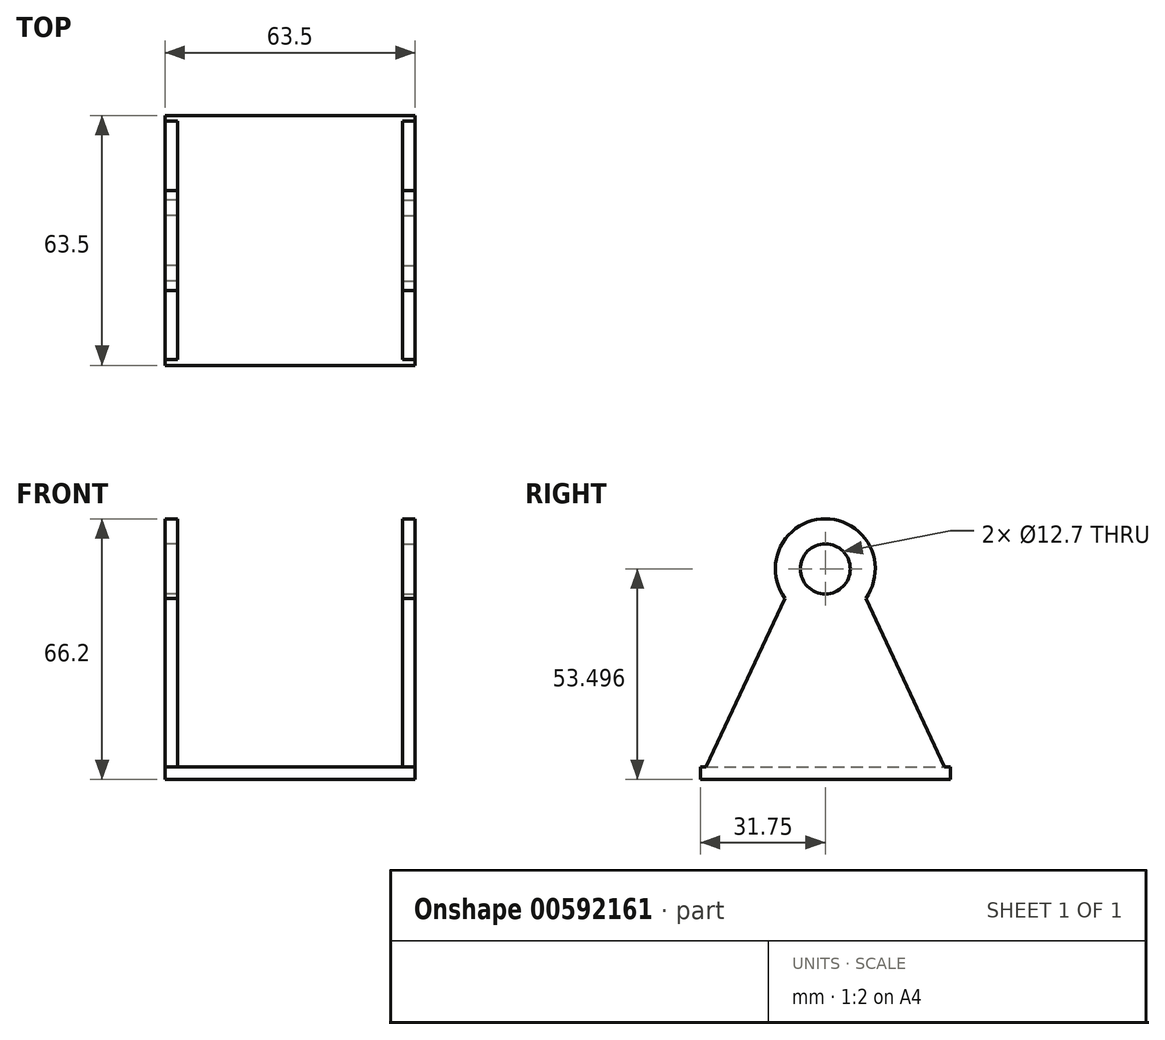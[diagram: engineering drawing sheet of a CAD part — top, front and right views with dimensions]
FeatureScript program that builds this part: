
annotation { "Feature Type Name" : "Feature", "Feature Type Description" : "" }
export const myFeature = defineFeature(function(context is Context, id is Id, definition is map)
    precondition{}
    {
        {
            var Q0;
            Q0=qCreatedBy(makeId("Top.planeOp"),FACE);
            var sketch = newSketch(context, id + "F0", { "sketchPlane" : qUnion([Q0])});
            skLineSegment(sketch, "E0.bottom", {"start": v(0, -31.75) * mm, "end": v(31.75, -31.75) * mm});
            skLineSegment(sketch, "E0.top", {"start": v(0, 31.75) * mm, "end": v(31.75, 31.75) * mm});
            skLineSegment(sketch, "E0.left", {"start": v(0, -31.75) * mm, "end": v(0, 31.75) * mm});
            skLineSegment(sketch, "E0.right", {"start": v(31.75, -31.75) * mm, "end": v(31.75, 31.75) * mm});
            skSolve(sketch);
        }
        {
            var Q0;
            Q0=makeQuery(id+"F0.imprint","IMPRINT",FACE,{"disambiguationData":[TD([[makeQuery(id+"F0.imprint","IMPRINT",EDGE,{"derivedFrom":sQuery(id+"F0.wireOp",EDGE,"E0.bottom")}),1.0]])]});
            extrude(context, id + "F1", {"entities" : qUnion([Q0]), "depth" : 3.17 * mm, "offsetDistance" : 25.4 * mm});
        }
        {
            var Q0;
            Q0=makeQuery(id+"F1.opExtrude","SWEPT_FACE",FACE,{"disambiguationData":[OSD([sQuery(id+"F0.wireOp",EDGE,"E0.right")])]});
            var sketch = newSketch(context, id + "F2", { "sketchPlane" : qUnion([Q0])});
            skLineSegment(sketch, "E1", {"start": v(-31.75, 0) * mm, "end": v(-10.28, 46.04) * mm});
            skLineSegment(sketch, "E2", {"start": v(31.75, 0) * mm, "end": v(10.28, 46.04) * mm});
            skLineSegment(sketch, "E3", {"start": v(-10.28, 46.04) * mm, "end": v(10.28, 46.04) * mm});
            skArc(sketch, "E4", {"start": v(10.28, 46.04) * mm, "mid": v(0, 66.2) * mm, "end": v(-10.28, 46.04) * mm});
            skCircle(sketch, "E5", {"center": v(0, 53.5) * mm, "radius": 6.35 * mm});
            skSolve(sketch);
        }
        {
            var Q0;
            {var subQ1=sQuery(id+"F2.wireOp",EDGE,"E3");Q0=makeQuery(id+"F2.imprint","IMPRINT",FACE,{"disambiguationData":[TD([[makeQuery(id+"F2.imprint","IMPRINT",EDGE,{"derivedFrom":subQ1}),-1.0]])]});}
            var Q1;
            Q1=makeQuery(id+"F2.imprint","IMPRINT",FACE,{"disambiguationData":[TD([[makeQuery(id+"F2.imprint","IMPRINT",EDGE,{"derivedFrom":sQuery(id+"F2.wireOp",EDGE,"E3")}),1.0]])]});
            extrude(context, id + "F3", {"entities" : qUnion([Q0, Q1]), "operationType" : NewBodyOperationType.ADD, "oppositeDirection" : true, "depth" : 3.17 * mm, "offsetDistance" : 25.4 * mm});
        }
        {
            var Q0;
            Q0=makeQuery(id+"F1.opExtrude","SWEPT_BODY",BODY,{"disambiguationData":[OSD([sQuery(id+"F0.wireOp",EDGE,"E0.bottom"),sQuery(id+"F0.wireOp",EDGE,"E0.top"),sQuery(id+"F0.wireOp",EDGE,"E0.left"),sQuery(id+"F0.wireOp",EDGE,"E0.right")])]});
            var Q1;
            Q1=qCreatedBy(makeId("Right.planeOp"),FACE);
            mirror(context, id + "F4", {"operationType" : NewBodyOperationType.ADD, "entities" : qUnion([Q0]), "mirrorPlane" : qUnion([Q1])});
        }
    });
